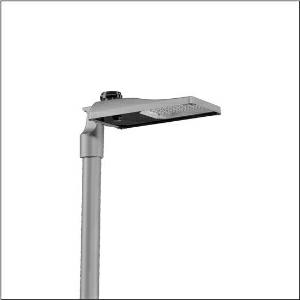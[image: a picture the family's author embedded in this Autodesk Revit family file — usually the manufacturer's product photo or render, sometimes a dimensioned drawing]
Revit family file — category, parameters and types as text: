
# Revit family: streetlight_sl_31_mini___st1_0a_5xh2d35m08ha_81d0
name_source: partatom
category: Lighting Fixtures
units: mm (PartAtom-declared; Revit-internal decimal feet)

## family parameters
Cut with Voids When Loaded = No
Host = Face
Light Source = No
Part Type = Normal
Room Calculation Point = No
Round Connector Dimension = Use Diameter
Shared = No

## types (1)
- --- (1 x LED, 9230 lm, 68.3 W, 3000K)
    Apparent Load = 68 VA
    CIE Flux Codes = 37 72 97 100 100
    Color Rendering = 70
    Color Temperature = 3000K
    Default Elevation = 1800 mm
    Description = Streetlight SL 31 mini NEMA (7pin), Desk-Remote mast luminaire for post-top, side-entry; light control with lens of PMMA; light distribution: ST1.0a, direct asymmetric distribution, for standard-compliant lighting for roads and squares; LED: luminous flux: 9.230lm, light colour: 730, colour temperature: 3000K; luminous efficacy: 135,1lm/W; control: pre-setting: linear dimming characteristic, flexible luminous flux parameterisation, time-dependent luminous flux control, constant luminous flux control, intelligent temperature release in ECG and LED module, overheat protection; luminaire housing, of diecast aluminium, Siteco® metallic grey (DB 702S), corrosivity category C5 high according to DIN EN ISO 12944; cover of toughened safety glass, transparent, mast flange of diecast aluminium, Siteco® metallic grey (DB 702S), spigot size: 76/60mm, mast flange included unmounted; with cable H07RN-F 3x 1.5mm², cable length: 8,5m, connection cable pre-assembled; mains connection: 220..240V, AC, 50/60Hz; power consumption (at start of service life): 68,3W / (at end of service life): 74,5W / (with reduced operation 50%): 29,5W; protection rating (complete): IP66; insulation class (complete): insulation class I (protective earthing); impact resistance: IK09; certification: CE, ENEC, ENEC+, VDE, UKCA; permissible operating ambient temperature for outdoor applications: -40..+50°C; packaging unit: 1 piece

Light Distribution: ST1.0a
    Height = 76 mm
    Lamp = 1 x LED
    Lamp Light Flux = 9230 lm
    Lamp Power = 68.3 W
    Lamp count = 1
    Length = 547 mm
    Luminous efficacy = 135 lm/W
    Manufacturer = Siteco
    ModVariant = No
    Model = 5XH2D35M08HA
    Number of Poles = 1
    OnlyDefault = Yes
    Power Factor = 1
    Product Name = Streetlight SL 31 mini | ST1.0a
    Product group = mast luminaire | pylon top
    ProductGroupID = 6100
    Protection Class = Protection class I
    Protection Degree = IP 66
    RLX_Detail_Level = 1
    RLX_Emergency_Light_Flux = 0 lm
    RLX_Emergency_Type = 0
    RLX_Emergency_Type_DB = No
    RlxData = <blob elided: 40061 chars, md5=4bbdc97f>
    Socket = socket
    Standby Power = 0 W
    System Light Flux = 9230 lm
    System Power = 68 W
    Type Comments = factory setting: luminous flux: 100 % | dim-lin: 254 | 692 mA
    Type Image = l_1300324.jpg
    URL = http://relux.com
    VarID = @adj_019417
    Voltage = 0 V
    Weight = 0.00 kg
    Width = 265 mm

## geometry (parser evidence)
native form markers: Blend x4, Sweep x9
no freeform markers — native parametric forms only
